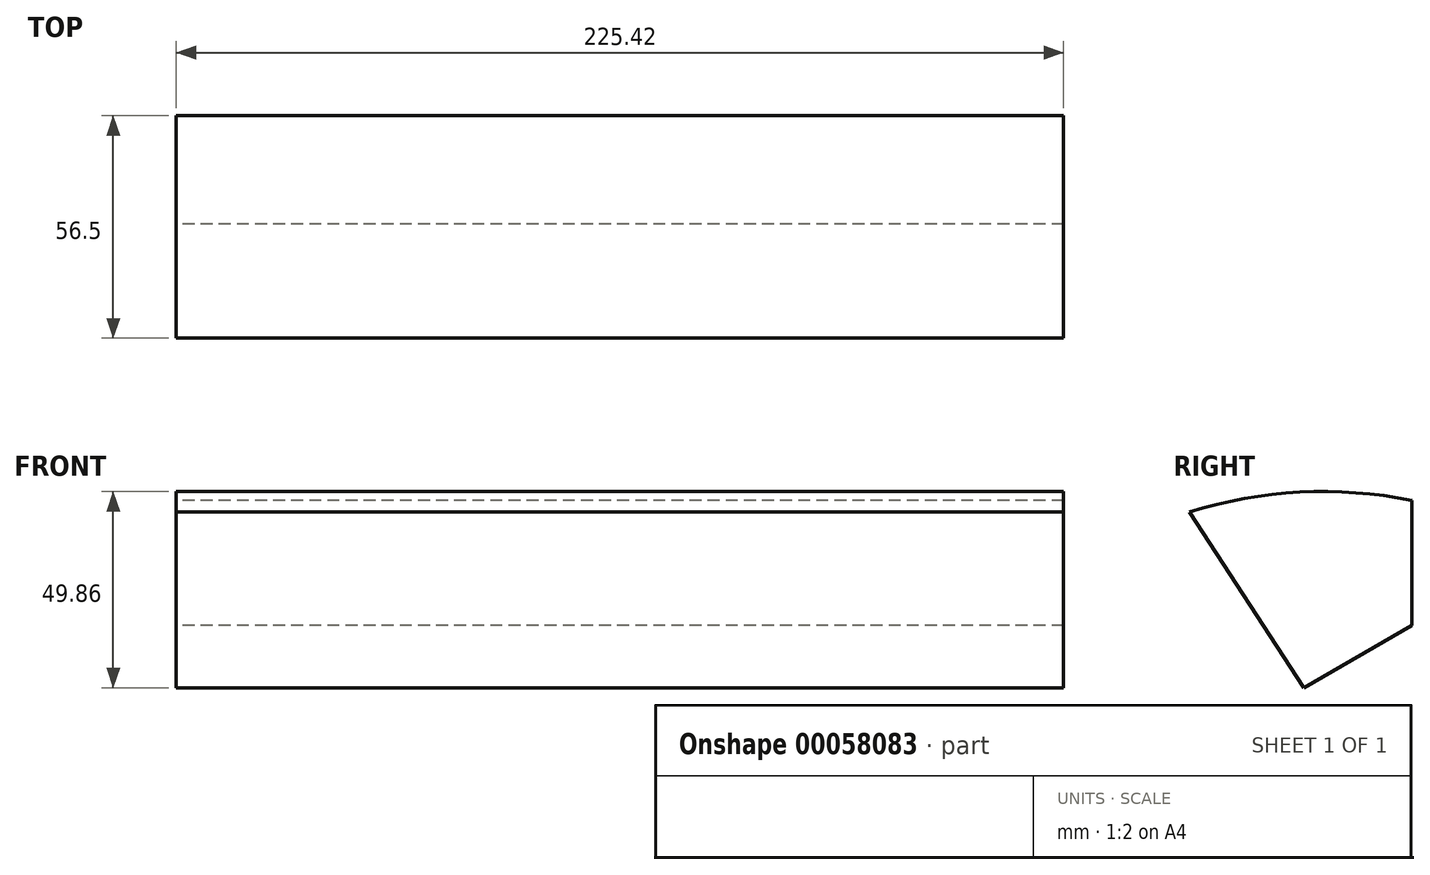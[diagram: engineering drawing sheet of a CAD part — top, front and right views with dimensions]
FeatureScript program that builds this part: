
annotation { "Feature Type Name" : "Feature", "Feature Type Description" : "" }
export const myFeature = defineFeature(function(context is Context, id is Id, definition is map)
    precondition{}
    {
        {
            var Q0;
            Q0=qCreatedBy(makeId("Right.planeOp"),FACE);
            var sketch = newSketch(context, id + "F0", { "sketchPlane" : qUnion([Q0])});
            skLineSegment(sketch, "E0", {"start": v(0, 0) * mm, "end": v(0, 31.75) * mm});
            skLineSegment(sketch, "E1", {"start": v(-56.5, 28.79) * mm, "end": v(-27.5, -15.88) * mm});
            skLineSegment(sketch, "E2", {"start": v(-27.5, -15.87) * mm, "end": v(0, 0) * mm});
            skArc(sketch, "E3", {"start": v(0, 31.75) * mm, "mid": v(-28.44, 33.82) * mm, "end": v(-56.5, 28.79) * mm});
            skLineSegment(sketch, "E4", {"start": v(0, 31.75) * mm, "end": v(-56.5, 28.79) * mm, "construction": true});
            skSolve(sketch);
        }
        {
            var Q0;
            Q0 = qSketchRegion(id + "F0", true);
            extrude(context, id + "F1", {"entities" : qUnion([Q0]), "endBound" : BoundingType.SYMMETRIC, "depth" : 225.42 * mm});
        }
    });
